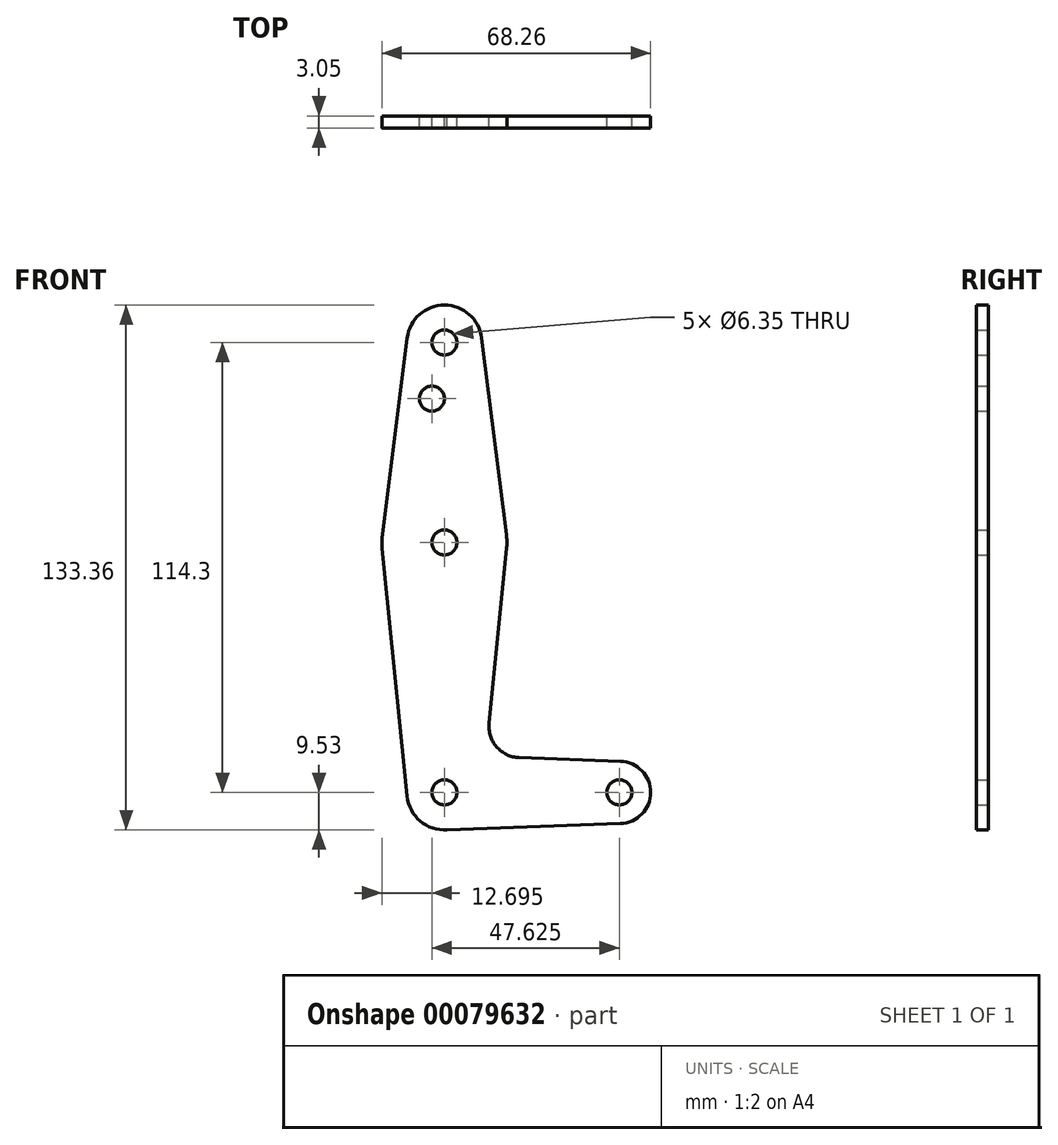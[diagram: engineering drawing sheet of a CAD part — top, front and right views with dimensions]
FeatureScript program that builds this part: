
annotation { "Feature Type Name" : "Feature", "Feature Type Description" : "" }
export const myFeature = defineFeature(function(context is Context, id is Id, definition is map)
    precondition{}
    {
        {
            var Q0;
            Q0=qCreatedBy(makeId("Front.planeOp"),FACE);
            var sketch = newSketch(context, id + "F0", { "sketchPlane" : qUnion([Q0])});
            skCircle(sketch, "E0", {"center": v(0, 0) * mm, "radius": 9.53 * mm});
            skCircle(sketch, "E1", {"center": v(0, 114.3) * mm, "radius": 9.53 * mm});
            skCircle(sketch, "E2", {"center": v(0, 63.5) * mm, "radius": 15.88 * mm});
            skCircle(sketch, "E3", {"center": v(44.45, 0) * mm, "radius": 7.94 * mm});
            skLineSegment(sketch, "E4", {"start": v(0, 114.3) * mm, "end": v(0, 0) * mm, "construction": true});
            skLineSegment(sketch, "E5", {"start": v(0, 0) * mm, "end": v(44.45, 0) * mm, "construction": true});
            skLineSegment(sketch, "E6", {"start": v(9.45, 115.5) * mm, "end": v(15.75, 65.48) * mm});
            skLineSegment(sketch, "E7", {"start": v(-9.45, 115.5) * mm, "end": v(-15.75, 65.48) * mm});
            skLineSegment(sketch, "E8", {"start": v(15.8, 61.91) * mm, "end": v(11.34, 17.59) * mm});
            skLineSegment(sketch, "E9", {"start": v(-15.8, 61.91) * mm, "end": v(-9.48, -0.95) * mm});
            skLineSegment(sketch, "E10", {"start": v(18.97, 8.85) * mm, "end": v(44.73, 7.93) * mm});
            skLineSegment(sketch, "E11", {"start": v(0, -9.53) * mm, "end": v(44.73, -7.93) * mm});
            skCircle(sketch, "E12", {"center": v(0, 114.3) * mm, "radius": 3.18 * mm});
            skCircle(sketch, "E13", {"center": v(0, 63.5) * mm, "radius": 3.18 * mm});
            skCircle(sketch, "E14", {"center": v(0, 0) * mm, "radius": 3.18 * mm});
            skCircle(sketch, "E15", {"center": v(44.45, 0) * mm, "radius": 3.18 * mm});
            skCircle(sketch, "E16", {"center": v(-3.17, 100.03) * mm, "radius": 3.18 * mm});
            skArc(sketch, "E17.filletArc", {"start": v(11.34, 17.59) * mm, "mid": v(13.26, 11.57) * mm, "end": v(18.97, 8.85) * mm});
            skSolve(sketch);
        }
        {
            var Q0;
            Q0 = qSketchRegion(id + "F0", true);
            extrude(context, id + "F1", {"entities" : qUnion([Q0]), "depth" : 3.05 * mm});
        }
    });
